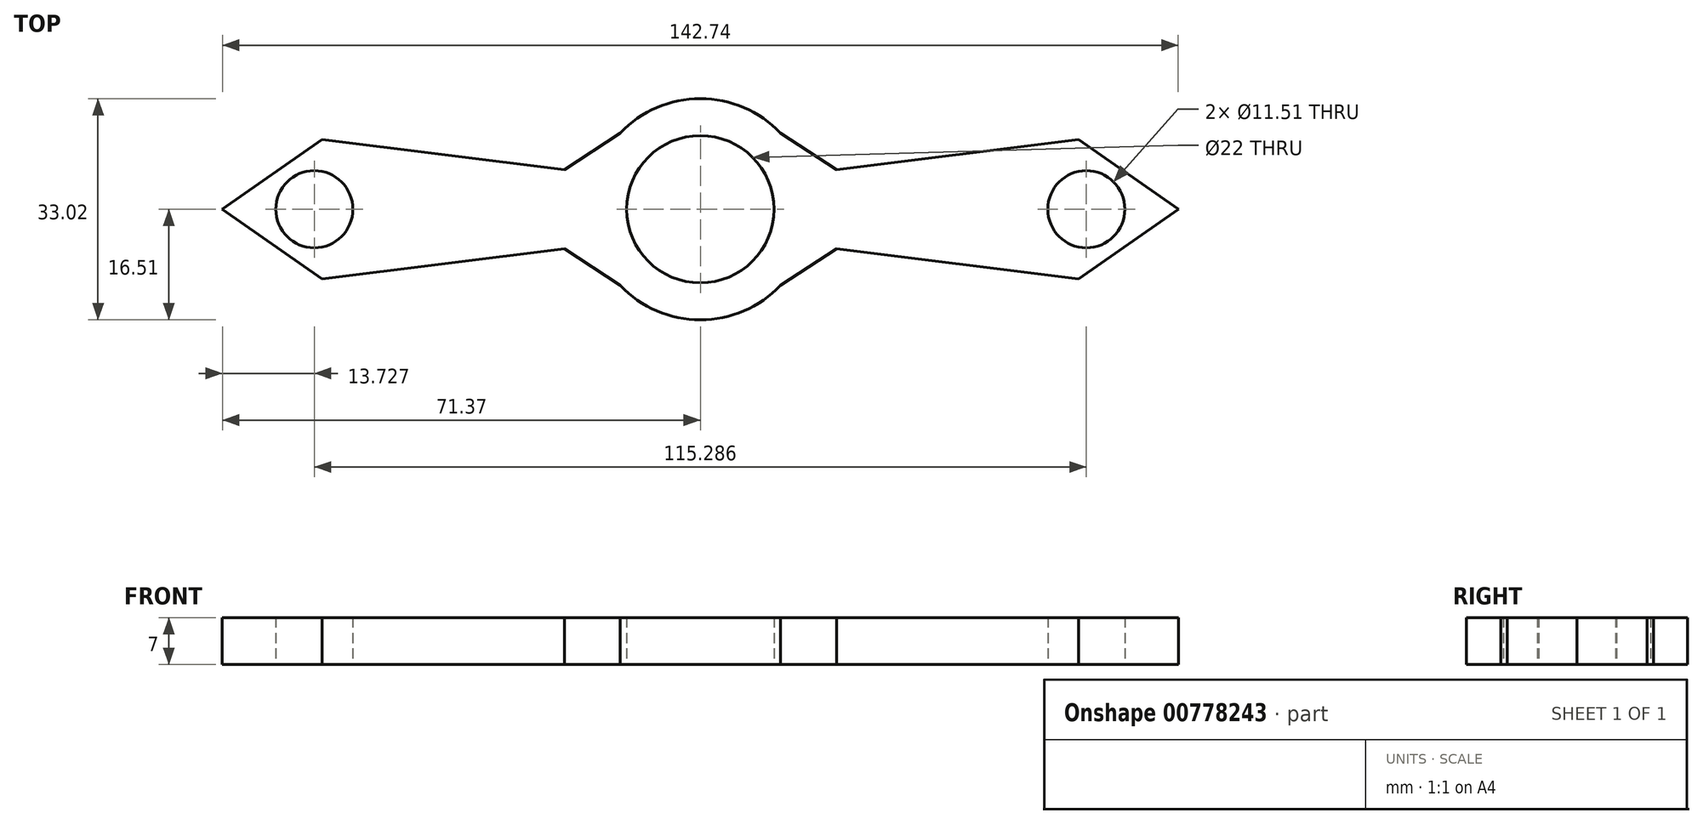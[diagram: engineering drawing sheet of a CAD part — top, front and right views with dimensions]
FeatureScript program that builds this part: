
annotation { "Feature Type Name" : "Feature", "Feature Type Description" : "" }
export const myFeature = defineFeature(function(context is Context, id is Id, definition is map)
    precondition{}
    {
        {
            var Q0;
            Q0=qCreatedBy(makeId("Top.planeOp"),FACE);
            var sketch = newSketch(context, id + "F0", { "sketchPlane" : qUnion([Q0])});
            skCircle(sketch, "E0", {"center": v(0, 0) * mm, "radius": 11 * mm});
            skArc(sketch, "E1", {"start": v(-11.95, -11.4) * mm, "mid": v(0, -16.51) * mm, "end": v(11.95, -11.4) * mm});
            skCircle(sketch, "E2", {"center": v(-57.64, 0) * mm, "radius": 5.76 * mm});
            skLineSegment(sketch, "E3", {"start": v(-11.95, 11.4) * mm, "end": v(-20.32, 5.92) * mm});
            skLineSegment(sketch, "E4", {"start": v(-20.32, 5.92) * mm, "end": v(-56.51, 10.44) * mm});
            skLineSegment(sketch, "E5", {"start": v(-56.51, 10.44) * mm, "end": v(-71.37, 0) * mm});
            skLineSegment(sketch, "E6.MirrorCS", {"start": v(-11.95, -11.4) * mm, "end": v(-20.32, -5.92) * mm});
            skLineSegment(sketch, "E7.MirrorCS", {"start": v(-56.51, -10.44) * mm, "end": v(-71.37, 0) * mm});
            skLineSegment(sketch, "E8.MirrorCS", {"start": v(-20.32, -5.92) * mm, "end": v(-56.51, -10.44) * mm});
            skCircle(sketch, "E9.MirrorC", {"center": v(57.64, 0) * mm, "radius": 5.76 * mm});
            skLineSegment(sketch, "E10.MirrorCS", {"start": v(56.51, -10.44) * mm, "end": v(71.37, 0) * mm});
            skLineSegment(sketch, "E11.MirrorCS", {"start": v(56.51, 10.44) * mm, "end": v(71.37, 0) * mm});
            skLineSegment(sketch, "E12.MirrorCS", {"start": v(11.95, -11.4) * mm, "end": v(20.32, -5.92) * mm});
            skLineSegment(sketch, "E13.MirrorCS", {"start": v(11.95, 11.4) * mm, "end": v(20.32, 5.92) * mm});
            skLineSegment(sketch, "E14.MirrorCS", {"start": v(20.32, -5.92) * mm, "end": v(56.51, -10.44) * mm});
            skLineSegment(sketch, "E15.MirrorCS", {"start": v(20.32, 5.92) * mm, "end": v(56.51, 10.44) * mm});
            skArc(sketch, "E16.trimOffspring", {"start": v(11.95, 11.4) * mm, "mid": v(0, 16.51) * mm, "end": v(-11.95, 11.4) * mm});
            skSolve(sketch);
        }
        {
            var Q0;
            Q0 = qSketchRegion(id + "F0", true);
            extrude(context, id + "F1", {"entities" : qUnion([Q0]), "endBound" : BoundingType.SYMMETRIC, "depth" : 7 * mm, "offsetDistance" : 25.4 * mm});
        }
    });
